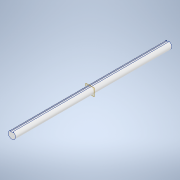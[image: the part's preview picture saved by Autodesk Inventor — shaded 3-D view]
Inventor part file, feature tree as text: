
AUTODESK INVENTOR PART (.ipt)
format: ipt  version: 2020.3 (Build 243373000, 373)  size: 101,888 bytes
history: native  units: in
note: dims shown in document units (in); Inventor stores cm internally (conversion verified against a paired STEP export)
features: extrude x1, sketch x1
ambient origin geometry x8: Origin, YZ Plane, XZ Plane, XY Plane, X Axis, Y Axis, Z Axis, Center Point
bodies: Solid1 (feature_tree)
feature tree (2):
  extrude  "Extrusion1"  Depth=8.0in
  sketch  "Sketch1"  dims[d0=0.375in d1=0.0469in d2=0.0628in d3=8.0in d4=0.0in]
